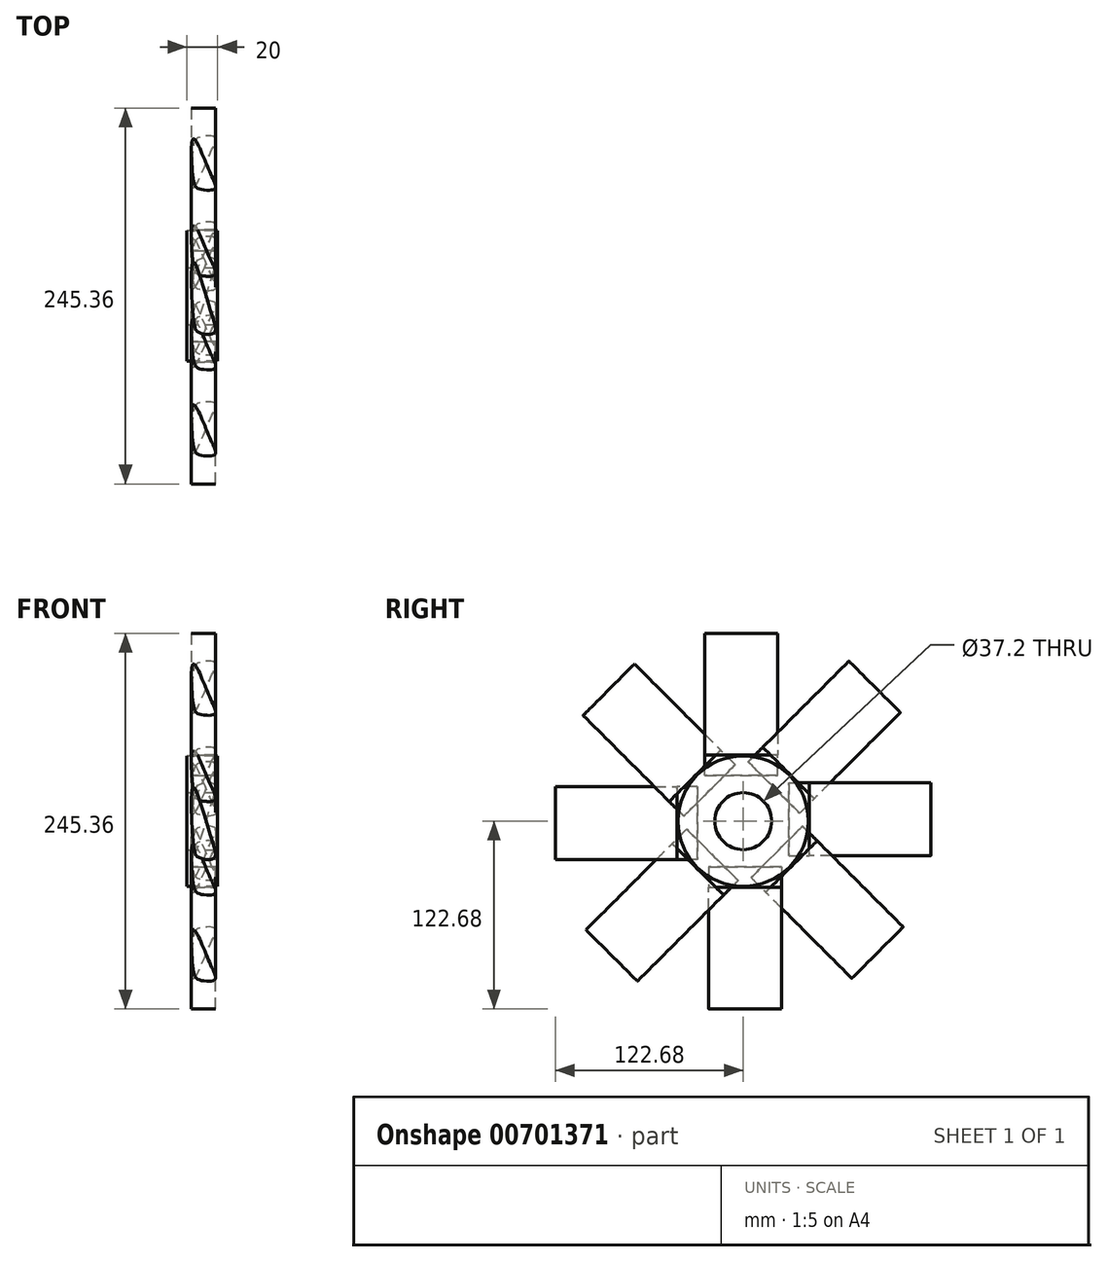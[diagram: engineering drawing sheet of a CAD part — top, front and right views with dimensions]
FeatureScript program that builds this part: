
annotation { "Feature Type Name" : "Feature", "Feature Type Description" : "" }
export const myFeature = defineFeature(function(context is Context, id is Id, definition is map)
    precondition{}
    {
        {
            var Q0;
            Q0=qCreatedBy(makeId("Right.planeOp"),FACE);
            var sketch = newSketch(context, id + "F0", { "sketchPlane" : qUnion([Q0])});
            skCircle(sketch, "E0", {"center": v(0, 0) * mm, "radius": 42.54 * mm});
            skSolve(sketch);
        }
        {
            var Q0;
            Q0=makeQuery(id+"F0.imprint","IMPRINT",FACE,{"disambiguationData":[TD([[makeQuery(id+"F0.imprint","IMPRINT",EDGE,{"derivedFrom":sQuery(id+"F0.wireOp",EDGE,"E0")}),1.0]])]});
            extrude(context, id + "F1", {"entities" : qUnion([Q0]), "depth" : 20 * mm, "offsetDistance" : 25.4 * mm});
        }
        {
            var Q0;
            Q0=qCreatedBy(makeId("Front.planeOp"),FACE);
            cPlane(context, id + "F2", {"entities" : qUnion([Q0]), "cplaneType" : CPlaneType.OFFSET, "offset" : 43.18 * mm, "width" : 152.4 * mm, "height" : 152.4 * mm});
        }
        {
            var Q0;
            Q0=qCreatedBy(id+"F2.planeOp",FACE);
            var sketch = newSketch(context, id + "F3", { "sketchPlane" : qUnion([Q0])});
            skFitSpline(sketch, "E1", {"points": [v(4.12, 22.37) * mm, v(15.4, -9.64) * mm, v(17.74, -24.24) * mm, v(8.14, -23.9) * mm, v(4.24, -15.41) * mm, v(4.12, 22.37) * mm]});
            skSolve(sketch);
        }
        {
            var Q0;
            Q0=makeQuery(id+"F3.imprint","IMPRINT",FACE,{"disambiguationData":[TD([[makeQuery(id+"F3.imprint","IMPRINT",EDGE,{"derivedFrom":sQuery(id+"F3.wireOp",EDGE,"E1")}),-1.0]])]});
            extrude(context, id + "F4", {"entities" : qUnion([Q0]), "depth" : 79.5 * mm, "offsetDistance" : 25.4 * mm});
        }
        {
            var Q0;
            Q0=makeQuery(id+"F4.opExtrude","CAP_FACE",FACE,{"disambiguationData":[OSD([sQuery(id+"F3.wireOp",EDGE,"E1")])],"isStart":true});
            extrude(context, id + "F5", {"entities" : qUnion([Q0]), "depth" : 13.46 * mm, "offsetDistance" : 25.4 * mm});
        }
        {
            var Q0;
            Q0=qCreatedBy(makeId("Front.planeOp"),FACE);
            var sketch = newSketch(context, id + "F6", { "sketchPlane" : qUnion([Q0])});
            skPoint(sketch, "E2.end.orphan", {"position": v(0, -16.46) * mm});
            skPoint(sketch, "E2.start.orphan", {"position": v(-47.51, 0) * mm});
            skLineSegment(sketch, "E3", {"start": v(-47.51, 0) * mm, "end": v(44.39, 0) * mm});
            skSolve(sketch);
        }
        {
            var Q0;
            Q0=makeQuery(id+"F5.opExtrude","SWEPT_BODY",BODY,{"disambiguationData":[OSD([sQuery(id+"F3.wireOp",EDGE,"E1")])]});
            var Q1;
            Q1=makeQuery(id+"F4.opExtrude","SWEPT_BODY",BODY,{"disambiguationData":[OSD([sQuery(id+"F3.wireOp",EDGE,"E1")])]});
            var Q2;
            Q2=sQuery(id+"F6.wireOp",EDGE,"E3");
            circularPattern(context, id + "F7", {"entities" : qUnion([Q0, Q1]), "axis" : qUnion([Q2]), "angle" : 360 * degree, "instanceCount" : 8, "equalSpace" : true});
        }
        {
            var Q0;
            Q0=makeQuery(id+"F1.opExtrude","CAP_FACE",FACE,{"disambiguationData":[OSD([sQuery(id+"F0.wireOp",EDGE,"E0")])],"isStart":true});
            var sketch = newSketch(context, id + "F8", { "sketchPlane" : qUnion([Q0])});
            skCircle(sketch, "E4", {"center": v(0, 0) * mm, "radius": 25 * mm});
            skSolve(sketch);
        }
        {
            var Q0;
            Q0=makeQuery(id+"F8.imprint","IMPRINT",FACE,{"disambiguationData":[TD([[makeQuery(id+"F8.imprint","IMPRINT",EDGE,{"derivedFrom":sQuery(id+"F8.wireOp",EDGE,"E4")}),1.0]])]});
            extrude(context, id + "F9", {"entities" : qUnion([Q0]), "operationType" : NewBodyOperationType.ADD, "oppositeDirection" : true, "depth" : 19.8 * mm, "offsetDistance" : 25.4 * mm});
        }
        {
            var Q0;
            Q0=makeQuery(id+"F1.opExtrude","CAP_FACE",FACE,{"disambiguationData":[OSD([sQuery(id+"F0.wireOp",EDGE,"E0")])],"isStart":false});
            var sketch = newSketch(context, id + "F10", { "sketchPlane" : qUnion([Q0])});
            skCircle(sketch, "E5", {"center": v(0, 0) * mm, "radius": 18.6 * mm});
            skSolve(sketch);
        }
        {
            var Q0;
            Q0=makeQuery(id+"F10.imprint","IMPRINT",FACE,{"disambiguationData":[TD([[makeQuery(id+"F10.imprint","IMPRINT",EDGE,{"derivedFrom":sQuery(id+"F10.wireOp",EDGE,"E5")}),1.0]])]});
            extrude(context, id + "F11", {"entities" : qUnion([Q0]), "operationType" : NewBodyOperationType.REMOVE, "oppositeDirection" : true, "depth" : 76.2 * mm, "offsetDistance" : 25.4 * mm});
        }
    });
